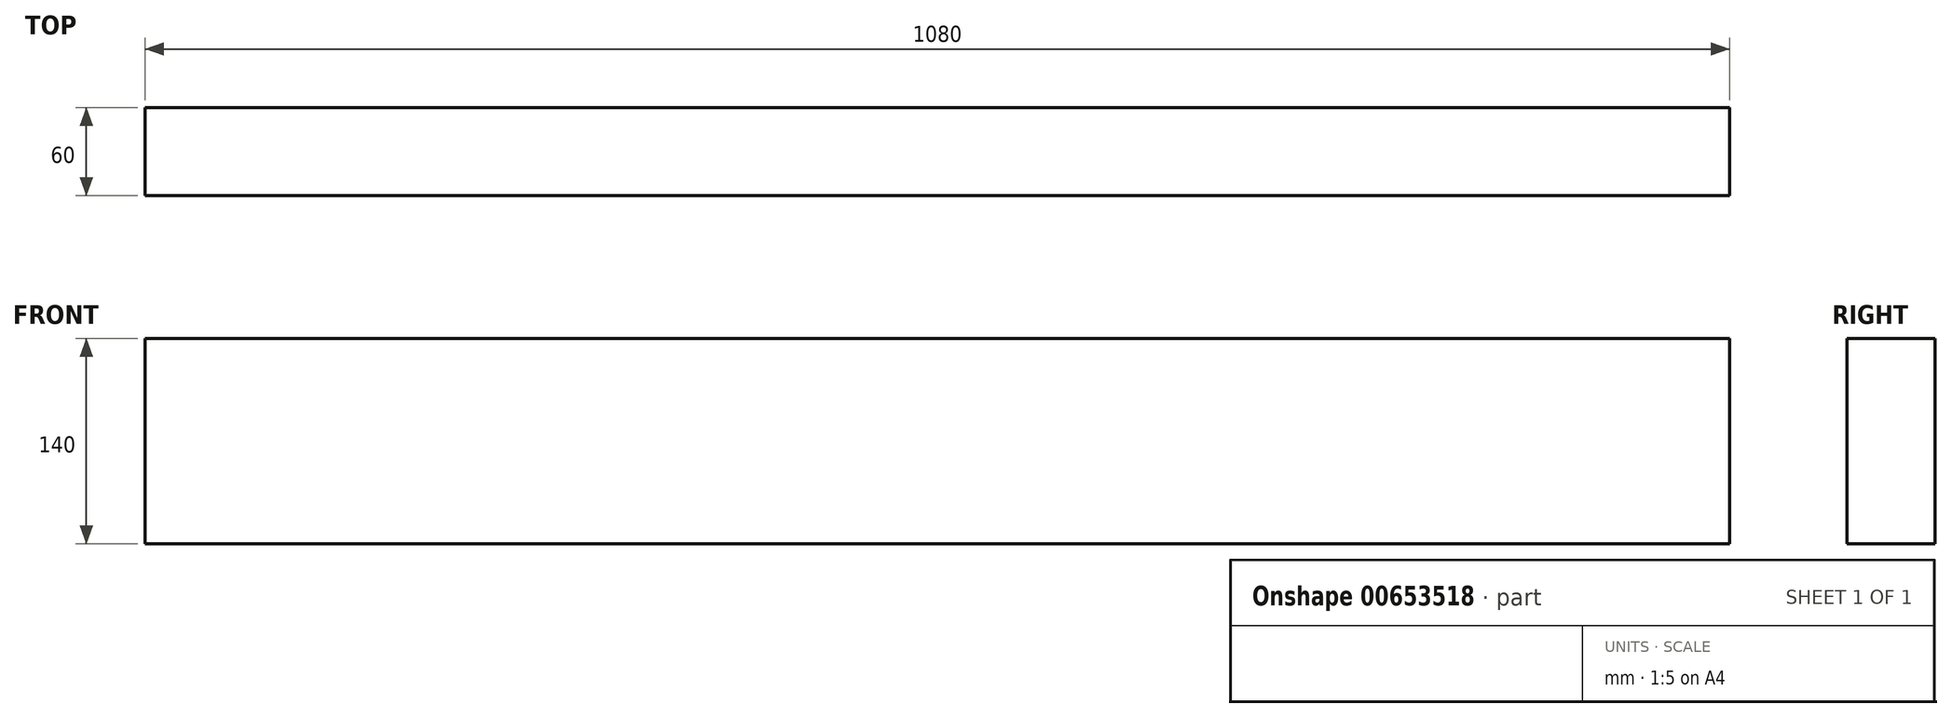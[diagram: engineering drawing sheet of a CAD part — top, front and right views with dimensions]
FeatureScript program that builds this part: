
annotation { "Feature Type Name" : "Feature", "Feature Type Description" : "" }
export const myFeature = defineFeature(function(context is Context, id is Id, definition is map)
    precondition{}
    {
        {
            var Q0;
            Q0=qCreatedBy(makeId("Right.planeOp"),FACE);
            var sketch = newSketch(context, id + "F0", { "sketchPlane" : qUnion([Q0])});
            skLineSegment(sketch, "E0.bottom", {"start": v(56.64, 144.08) * mm, "end": v(-3.36, 144.08) * mm});
            skLineSegment(sketch, "E0.top", {"start": v(56.64, 4.08) * mm, "end": v(-3.36, 4.08) * mm});
            skLineSegment(sketch, "E0.left", {"start": v(56.64, 144.08) * mm, "end": v(56.64, 4.08) * mm});
            skLineSegment(sketch, "E0.right", {"start": v(-3.36, 144.08) * mm, "end": v(-3.36, 4.08) * mm});
            skSolve(sketch);
        }
        {
            var Q0;
            Q0=makeQuery(id+"F0.imprint","IMPRINT",FACE,{"disambiguationData":[TD([[makeQuery(id+"F0.imprint","IMPRINT",EDGE,{"derivedFrom":sQuery(id+"F0.wireOp",EDGE,"E0.bottom")}),1.0]])]});
            extrude(context, id + "F1", {"entities" : qUnion([Q0]), "depth" : 1080 * mm, "offsetDistance" : 25 * mm});
        }
    });
